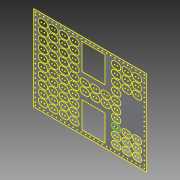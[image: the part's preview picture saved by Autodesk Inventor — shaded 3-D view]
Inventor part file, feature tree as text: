
AUTODESK INVENTOR PART (.ipt)
format: ipt  version: 2014 SP1 (Build 180222100, 222)  size: 1,352,704 bytes
history: native  units: in
note: dims shown in document units (in); Inventor stores cm internally (conversion verified against a paired STEP export)
features: sketch x10, other x8, sheet_metal_op x5, pattern_linear x4, reference x4
ambient origin geometry x8: Origin, YZ Plane, XZ Plane, XY Plane, X Axis, Y Axis, Z Axis, Center Point
bodies: Solid1 (feature_tree)
feature tree (31):
  sheet_metal_op  "Face1"
  pattern_linear  "Rectangular Pattern2"  Count1=27 Spacing1=1.0in
  pattern_linear  "Rectangular Pattern3"  Spacing1=1.0in  [1 undecoded]
  sheet_metal_op  "Face2"
  sheet_metal_op  "Face3"
  pattern_linear  "Rectangular Pattern4"  Spacing1=1.8325in  [1 undecoded]
  pattern_linear  "Rectangular Pattern5"  Spacing1=0.125in  [1 undecoded]
  sketch  "Sketch13"  dims[d22=1.0in]
  sketch  "Sketch14"  dims[d23=1.0in d24=1.0in d25=1.8325in d28=0.125in d29=0.0625in d30=0.0in d31=3.937in d33=1.8325in d34=3.937in d36=2.5in d44=1.5748in d46=2.5in d47=1.5748in d49=1.8325in d52=1.5748in d54=1.8325in d55=1.5748in d57=2.5in d60=0.0625in d61=0.0625in d62=0.0312in d63=0.125in d64=0.0625in d65=0.0625in d66=0.0in d67=0.0625in d68=0.0625in d69=0.0312in d70=0.125in d71=0.0625in d72=0.7874in d74=2.5in d75=1.5748in d77=1.8325in d78=11.55in d79=5.5in d80=11.55in d81=0.7874in d83=2.5in d84=0.3937in d86=1.0in d88=3.937in d90=1.8325in d91=0.3937in d93=1.0in d95=0.0625in d96=0.0in d97=0.0625in d98=0.0in d99=7.4803in d101=1.0in d102=0.7874in d104=26.0in]
  sketch  "Sketch1"  dims[d0=27.0in]
  other  "Plate1"
  sketch  "Sketch2"  dims[d1=20.325in]
  sketch  "Sketch4"  dims[d2=0.0625in]
  reference  "Reference4"
  reference  "Reference5"
  sketch  "Sketch5"  dims[d4=7.25in]
  sketch  "Sketch7"  dims[d5=5.5in]
  other  "Plate2"
  sheet_metal_op  "Bend1"
  sketch  "Sketch8"  dims[d6=7.25in]
  other  "Plate3"
  sheet_metal_op  "Bend2"
  sketch  "Sketch10"  dims[d17=0.0625in]
  sketch  "Sketch12"  dims[d18=0.0in d19=10.6299in d21=1.0in]
  reference  "Reference10"
  reference  "Reference11"
  other  "Cut3"
  other  "Cut5"
  other  "Cut6"
  other  "Cut7"
  other  "Cut8"
note: 3 required parameter values undecoded (feature->parameter linkage not recoverable at this tier; creation-order binding heuristic only, values carry confidence <= 0.55)
